# Revit family: Toilet-Partition
name_source: partatom
category: Specialty Equipment
units: mm (PartAtom-declared; Revit-internal decimal feet)

## family parameters
Always vertical = Yes
Classification Number = 23.25.40.14.14.11
Cut with Voids When Loaded = No
Enable Cutting in Views = No
Maintain Annotation Orientation = No
Part Type = Normal
Room Calculation Point = No
Round Connector Dimension = Use Diameter
Shared = No
Work Plane-Based = No

## types (12) — shared parameters
Assembly Code = C1010400
Construction Details = http://www.arcat.com
Default Elevation = 0' - 0"
Expected Lifespan (Years) = 15
Fasteners = Tamper resistant stainless steel screws w/ nylon anchors
Green Building-LEED = http://www.arcat.com
Height = 5' - 11"
Keynote = 10150
Lock = Quarter Turn Slide Latch - Emergency Access by lifting door
Maintenance Schedule (Months) = 12
Manufacturer = Generic
Manufacturer Fax = (203) 939-2444
Manufacturer Website = http://www.arcat.com
Model = Generic
Product Data = http://www.arcat.com
Product Properties = http://www.arcat.com
Specification = http://www.arcat.com
Warranty Duration (Years) = 5

## per-type parameters (varying)
| type | Description | Door Opening | Stall Depth | Width |
| 36x57 | 36x57 Toilet Partition | 2' - 7 3/4" | 5' - 0" | 3' - 0" |
| 34x57 | 34x57 Toilet Partition | 2' - 5 3/4" | 4' - 9" | 2' - 10" |
| 32x57 | 32x57 Toilet Partition | 2' - 3 3/4" | 4' - 9" | 2' - 8" |
| 30x57 | 30x57 Toilet Partition | 2' - 1 3/4" | 4' - 9" | 2' - 6" |
| 36x54 | 36x54 Toilet Partition | 2' - 7 3/4" | 4' - 6" | 3' - 0" |
| 34x54 | 34x54 Toilet Partition | 2' - 5 3/4" | 4' - 6" | 2' - 10" |
| 32x54 | 32x54 Toilet Partition | 2' - 3 3/4" | 4' - 6" | 2' - 8" |
| 30x54 | 30x54 Toilet Partition | 2' - 1 3/4" | 4' - 6" | 2' - 6" |
| 36x48 | 36x48 Toilet Partition | 2' - 7 3/4" | 4' - 0" | 3' - 0" |
| 34x48 | 34x48 Toilet Partition | 2' - 5 3/4" | 4' - 0" | 2' - 10" |
| 32x48 | 32x48 Toilet Partition | 2' - 3 3/4" | 4' - 0" | 2' - 8" |
| 30x48 | 30x48 Toilet Partition | 2' - 1 3/4" | 4' - 0" | 2' - 6" |

## geometry (parser evidence)
native form markers: Sweep x4
no freeform markers — native parametric forms only
